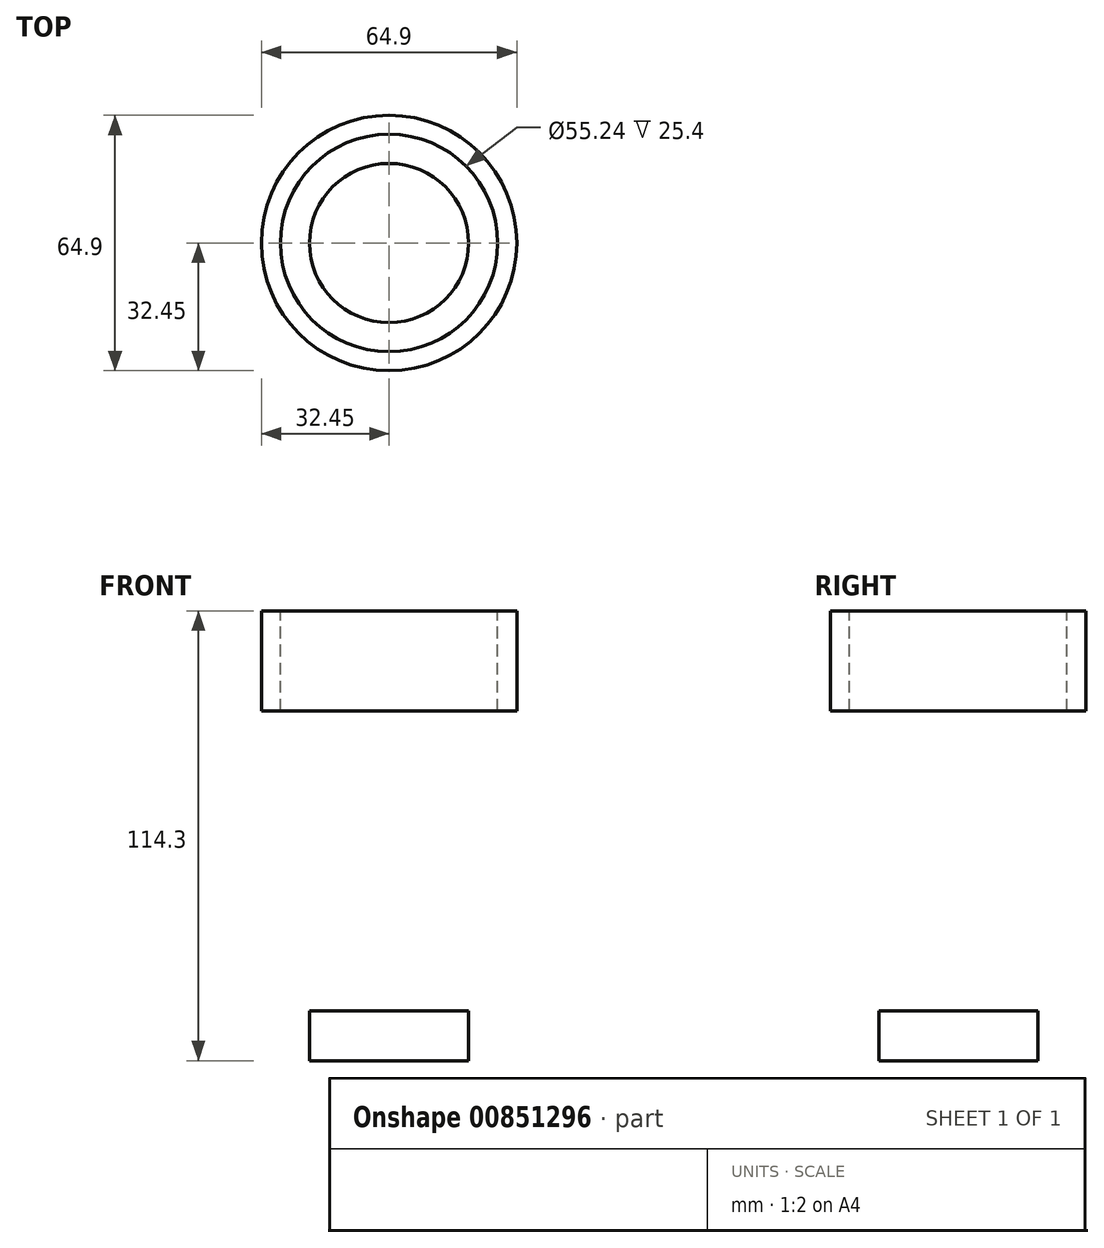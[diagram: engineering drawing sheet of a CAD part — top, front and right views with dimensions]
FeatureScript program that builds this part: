
annotation { "Feature Type Name" : "Feature", "Feature Type Description" : "" }
export const myFeature = defineFeature(function(context is Context, id is Id, definition is map)
    precondition{}
    {
        {
            var Q0;
            Q0=qCreatedBy(makeId("Top.planeOp"),FACE);
            var sketch = newSketch(context, id + "F0", { "sketchPlane" : qUnion([Q0])});
            skCircle(sketch, "E0", {"center": v(0, 0) * mm, "radius": 20.2 * mm});
            skSolve(sketch);
        }
        {
            var Q0;
            Q0=makeQuery(id+"F0.imprint","IMPRINT",FACE,{"disambiguationData":[TD([[makeQuery(id+"F0.imprint","IMPRINT",EDGE,{"derivedFrom":sQuery(id+"F0.wireOp",EDGE,"E0")}),1.0]])]});
            extrude(context, id + "F1", {"entities" : qUnion([Q0]), "depth" : 12.7 * mm, "offsetDistance" : 25.4 * mm});
        }
        {
            var Q0;
            Q0=makeQuery(id+"F1.opExtrude","CAP_FACE",FACE,{"disambiguationData":[OSD([sQuery(id+"F0.wireOp",EDGE,"E0")])],"isStart":false});
            cPlane(context, id + "F2", {"entities" : qUnion([Q0]), "cplaneType" : CPlaneType.OFFSET, "offset" : 76.2 * mm, "width" : 152.4 * mm, "height" : 152.4 * mm});
        }
        {
            var Q0;
            Q0=qCreatedBy(id+"F2.planeOp",FACE);
            var sketch = newSketch(context, id + "F3", { "sketchPlane" : qUnion([Q0])});
            skCircle(sketch, "E1", {"center": v(0, 0) * mm, "radius": 32.45 * mm});
            skSolve(sketch);
        }
        {
            var Q0;
            Q0=makeQuery(id+"F3.imprint","IMPRINT",FACE,{"disambiguationData":[TD([[makeQuery(id+"F3.imprint","IMPRINT",EDGE,{"derivedFrom":sQuery(id+"F3.wireOp",EDGE,"E1")}),1.0]])]});
            extrude(context, id + "F4", {"entities" : qUnion([Q0]), "depth" : 25.4 * mm, "offsetDistance" : 25.4 * mm});
        }
        {
            var Q0;
            Q0=makeQuery(id+"F1.opExtrude","CAP_FACE",FACE,{"disambiguationData":[OSD([sQuery(id+"F0.wireOp",EDGE,"E0")])],"isStart":false});
            var Q1;
            Q1=makeQuery(id+"F4.opExtrude","SWEPT_FACE",FACE,{"disambiguationData":[OSD([sQuery(id+"F3.wireOp",EDGE,"E1")])]});
            var Q2;
            Q2=makeQuery(id+"F1.opExtrude","CAP_FACE",FACE,{"disambiguationData":[OSD([sQuery(id+"F0.wireOp",EDGE,"E0")])],"isStart":false});
            var Q3;
            Q3=makeQuery(id+"F4.opExtrude","CAP_FACE",FACE,{"disambiguationData":[OSD([sQuery(id+"F3.wireOp",EDGE,"E1")])],"isStart":true});
            loft(context, id + "F5", {"bodyType" : ToolBodyType.SURFACE, "sheetProfilesArray" : [{ "sheetProfileEntities" : qUnion([Q0]) }, { "sheetProfileEntities" : qUnion([Q1]) }], "wireProfilesArray" : [{ "wireProfileEntities" : qUnion([Q2]) }, { "wireProfileEntities" : qUnion([Q3]) }]});
        }
        {
            var Q0;
            Q0=makeQuery(id+"F4.opExtrude","CAP_FACE",FACE,{"disambiguationData":[OSD([sQuery(id+"F3.wireOp",EDGE,"E1")])],"isStart":false});
            var sketch = newSketch(context, id + "F6", { "sketchPlane" : qUnion([Q0])});
            skCircle(sketch, "E2", {"center": v(0, 0) * mm, "radius": 27.62 * mm});
            skSolve(sketch);
        }
        {
            var Q0;
            Q0 = qSketchRegion(id + "F6", true);
            extrude(context, id + "F7", {"entities" : qUnion([Q0]), "operationType" : NewBodyOperationType.REMOVE, "oppositeDirection" : true, "depth" : 25.4 * mm, "offsetDistance" : 25.4 * mm});
        }
    });
